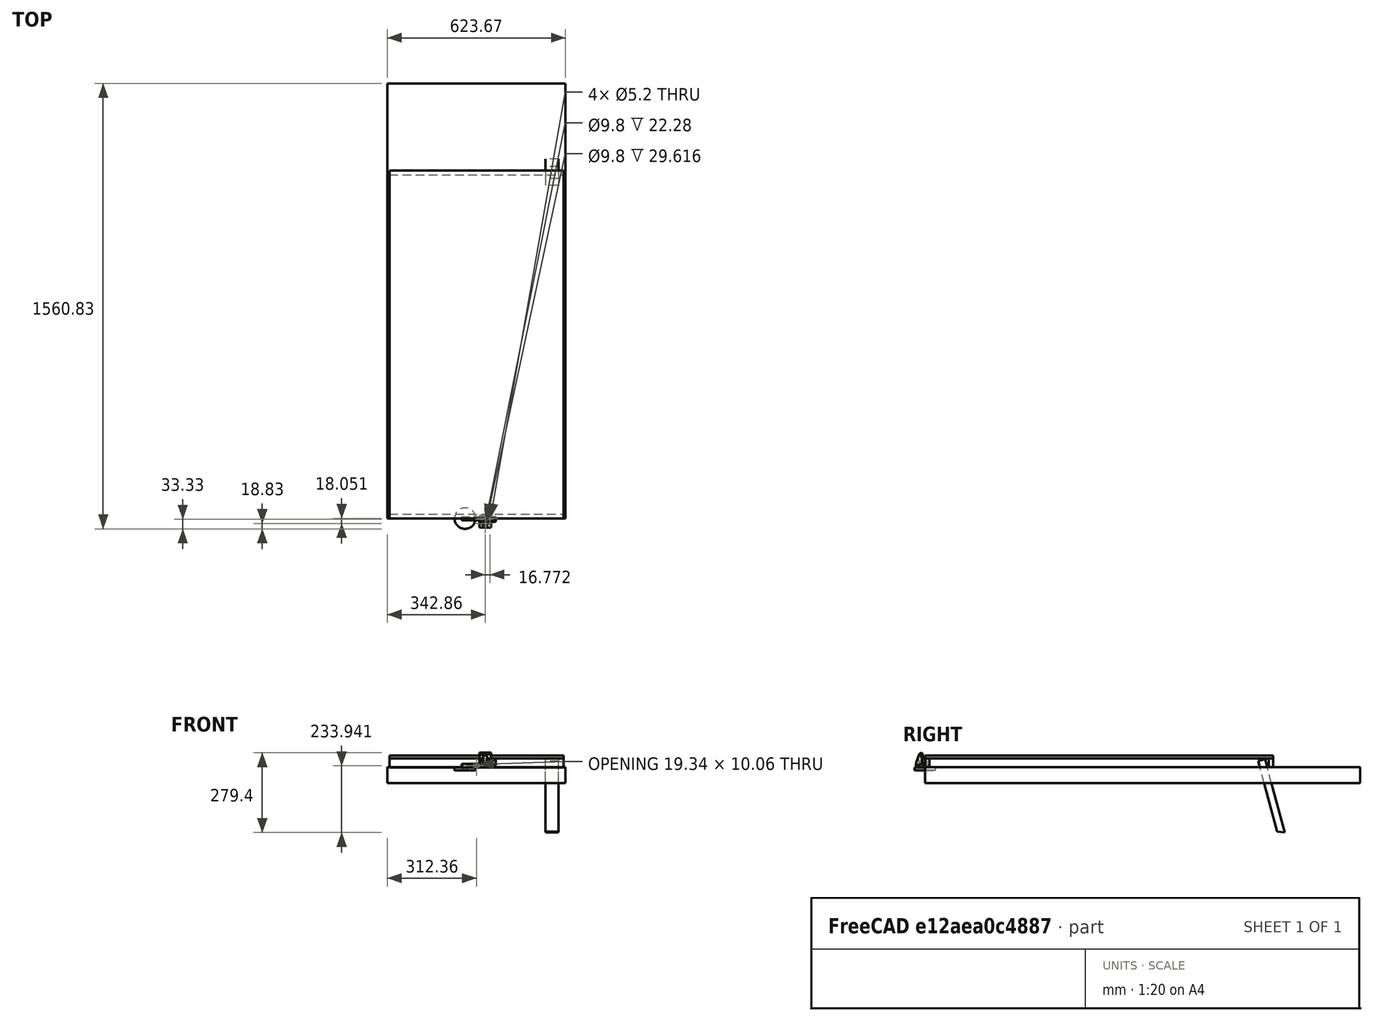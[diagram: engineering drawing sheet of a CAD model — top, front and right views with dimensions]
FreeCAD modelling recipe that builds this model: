
FCSTD DOCUMENT  (FreeCAD 0.21R)
Label: BoardModel
License: All rights reserved
LicenseURL: http://en.wikipedia.org/wiki/All_rights_reserved
objects: Sketcher::SketchObject×23, PartDesign::Pocket×12, PartDesign::Pad×11, PartDesign::Body×9, Part::FeaturePython×4, App::Part×4, App::Link×3, Mesh::Feature×2
note: 82 computed .brp shape members not serialized (recipe doc carries the construction recipe); baked Part::Feature solids carry a one-line shape summary decoded from their .brp

FEATURE [Sketcher::SketchObject] Sketch
  FullyConstrained = true
  MapMode = 5
  Support = -> [XY_Plane]
  sketch-geometry (10):
    g0: LineSegment StartX=-52.3875 StartY=6.35 StartZ=0 EndX=52.3875 EndY=6.35 EndZ=0
    g1: LineSegment StartX=52.3875 StartY=6.35 StartZ=0 EndX=52.3875 EndY=-6.35 EndZ=0
    g2: LineSegment StartX=52.3875 StartY=-6.35 StartZ=0 EndX=-52.3875 EndY=-6.35 EndZ=0
    g3: LineSegment StartX=-52.3875 StartY=-6.35 StartZ=0 EndX=-52.3875 EndY=6.35 EndZ=0
    g4: Circle CenterX=-47.3875 CenterY=0 CenterZ=0 NormalX=0 NormalY=0 NormalZ=1 AngleXU=0 Radius=2.5
    g5: Circle CenterX=-32.8875 CenterY=0 CenterZ=0 NormalX=0 NormalY=0 NormalZ=1 AngleXU=0 Radius=2.5
    g6: Circle CenterX=32.8875 CenterY=0 CenterZ=0 NormalX=0 NormalY=0 NormalZ=1 AngleXU=0 Radius=2
    g7: Circle CenterX=47.3875 CenterY=0 CenterZ=0 NormalX=0 NormalY=0 NormalZ=1 AngleXU=0 Radius=2
    g8: LineSegment StartX=-47.3875 StartY=0 StartZ=0 EndX=-32.8875 EndY=0 EndZ=0
    g9: LineSegment StartX=32.8875 StartY=0 StartZ=0 EndX=47.3875 EndY=0 EndZ=0
  constraints (26):
    c: Coincident(g0,g1)
    c: Coincident(g1,g2)
    c: Coincident(g2,g3)
    c: Coincident(g3,g0)
    c: Horizontal(g2)
    c: Vertical(g1)
    c: Symmetric(g0,g0,g-2)
    c: DistanceY(g3,g3) = 12.7
    c: Symmetric(g0,g2,g-1)
    c: DistanceX(g0,g0) = 104.775
    c: PointOnObject(g4,g-1)
    c: PointOnObject(g5,g-1)
    c: PointOnObject(g6,g-1)
    c: PointOnObject(g7,g-1)
    c: Diameter(g6) = 4
    c: Equal(g7,g6)
    c: Equal(g5,g4)
    c: Coincident(g8,g4)
    c: Coincident(g8,g5)
    c: Coincident(g9,g6)
    c: Coincident(g9,g7)
    c: Equal(g9,g8)
    c: Diameter(g5) = 5
    c: DistanceX(g8,g8) = 14.5
    c: DistanceX(g0,g4) = 5
    c: DistanceX(g7,g0) = 5
FEATURE [PartDesign::Pad] Pad
  Direction = (0,0,1)
  Length = 12.7
  Length2 = 10
  Profile = -> Sketch
  ReferenceAxis = -> Sketch [N_Axis]
  Type = 0
FEATURE [Sketcher::SketchObject] Sketch001
  FullyConstrained = false
  MapMode = 5
  Support = -> [XY_Plane001]
  sketch-geometry (3):
    g0: Circle CenterX=0 CenterY=0 CenterZ=0 NormalX=0 NormalY=0 NormalZ=1 AngleXU=0 Radius=36.8321
    g1: Circle CenterX=-7.25 CenterY=0 CenterZ=0 NormalX=0 NormalY=0 NormalZ=1 AngleXU=0 Radius=2.1
    g2: Circle CenterX=7.25 CenterY=0 CenterZ=0 NormalX=0 NormalY=0 NormalZ=1 AngleXU=0 Radius=2.1
  constraints (6):
    c: Coincident(g0,g-1)
    c: PointOnObject(g1,g-1)
    c: Equal(g1,g2)
    c: Symmetric(g1,g2,g0)
    c: DistanceX(g1,g2) = 14.5
    c: Diameter(g2) = 4.2
FEATURE [Sketcher::SketchObject] Sketch002
  FullyConstrained = true
  MapMode = 5
  Placement = pos=(0,0,0) rot=(0.57735,0.57735,0.57735;2.0944rad)
  Support = -> [YZ_Plane003]
  sketch-geometry (4):
    g0: LineSegment StartX=0 StartY=0 StartZ=0 EndX=15.24 EndY=0 EndZ=0
    g1: LineSegment StartX=15.24 StartY=0 StartZ=0 EndX=15.24 EndY=31.75 EndZ=0
    g2: LineSegment StartX=15.24 StartY=31.75 StartZ=0 EndX=0 EndY=31.75 EndZ=0
    g3: LineSegment StartX=0 StartY=31.75 StartZ=0 EndX=0 EndY=0 EndZ=0
  constraints (11):
    c: Coincident(g0,g1)
    c: Coincident(g1,g2)
    c: Coincident(g2,g3)
    c: Coincident(g3,g0)
    c: Horizontal(g0)
    c: Horizontal(g2)
    c: Vertical(g1)
    c: Vertical(g3)
    c: Coincident(g0,g-1)
    c: DistanceY(g3,g3) = 31.75
    c: DistanceX(g0,g0) = 15.24
FEATURE [PartDesign::Pad] Pad001
  Direction = (1,-2e-16,3e-16)
  Length = 609.6
  Length2 = 10
  Midplane = true
  Placement = pos=(0,0,0) rot=(0.57735,0.57735,0.57735;2.0944rad)
  Profile = -> Sketch002
  ReferenceAxis = -> Sketch002 [N_Axis]
  Type = 0
FEATURE [PartDesign::Body] Body002  label="Front"
  Group = -> [Sketch002,Pad001]
  Origin = -> Origin003
  Tip = -> Pad001
FEATURE [PartDesign::Pad] Pad002
  Direction = (0,0,1)
  Length = 10
  Length2 = 10
  Profile = -> Sketch001
  ReferenceAxis = -> Sketch001 [N_Axis]
  Reversed = true
  Type = 0
FEATURE [Sketcher::SketchObject] Sketch003
  AttachmentOffset = pos=(0,0,31.75) rot=(0,0,1;0rad)
  FullyConstrained = true
  MapMode = 5
  Placement = pos=(0,0,31.75) rot=(0,0,1;0rad)
  Support = -> [XY_Plane005]
  sketch-geometry (4):
    g0: LineSegment StartX=-304.8 StartY=0 StartZ=0 EndX=304.8 EndY=0 EndZ=0
    g1: LineSegment StartX=304.8 StartY=0 StartZ=0 EndX=304.8 EndY=1219.2 EndZ=0
    g2: LineSegment StartX=304.8 StartY=1219.2 StartZ=0 EndX=-304.8 EndY=1219.2 EndZ=0
    g3: LineSegment StartX=-304.8 StartY=1219.2 StartZ=0 EndX=-304.8 EndY=0 EndZ=0
  constraints (11):
    c: Coincident(g0,g1)
    c: Coincident(g1,g2)
    c: Coincident(g2,g3)
    c: Coincident(g3,g0)
    c: Horizontal(g2)
    c: Vertical(g1)
    c: Vertical(g3)
    c: Symmetric(g0,g0,g-2)
    c: DistanceX(g0,g0) = 609.6
    c: DistanceY(g3,g3) = 1219.2
    c: PointOnObject(g0,g-1)
FEATURE [PartDesign::Pad] Pad003
  Direction = (0,0,1)
  Length = 10
  Length2 = 10
  Profile = -> Sketch003
  ReferenceAxis = -> Sketch003 [N_Axis]
  Type = 0
FEATURE [PartDesign::Body] Body003  label="Top"
  Group = -> [Sketch003,Pad003]
  Origin = -> Origin005
  Tip = -> Pad003
FEATURE [Sketcher::SketchObject] Sketch004
  FullyConstrained = false
  MapMode = 5
  Placement = pos=(0,0,0) rot=(0.57735,0.57735,0.57735;2.0944rad)
  Support = -> [YZ_Plane006]
  sketch-geometry (8):
    g0: LineSegment StartX=-1.51635 StartY=-5.19268 StartZ=0 EndX=-5.92453 EndY=19.8073 EndZ=0
    g1: LineSegment StartX=12.7 StartY=8 StartZ=0 EndX=12.7 EndY=0 EndZ=0
    g2: LineSegment StartX=0 StartY=0 StartZ=0 EndX=12.7 EndY=0 EndZ=0
    g3: LineSegment StartX=12.7 StartY=8 StartZ=0 EndX=0.357421 EndY=8 EndZ=0
    g4: LineSegment StartX=0.357421 StartY=8 StartZ=0 EndX=-1.72453 EndY=19.8073 EndZ=0
    g5: LineSegment StartX=-1.72453 StartY=19.8073 StartZ=0 EndX=-5.92453 EndY=19.8073 EndZ=0
    g6: LineSegment StartX=-1.51635 StartY=-5.19268 StartZ=0 EndX=0 EndY=-5.19268 EndZ=0
    g7: LineSegment StartX=0 StartY=-5.19268 StartZ=0 EndX=0 EndY=0 EndZ=0
  constraints (21):
    c: PointOnObject(g1,g-1)
    c: Vertical(g1)
    c: Coincident(g1,g2)
    c: Angle(g-1,g0) = 1.74533
    c: DistanceY(g0,g0) = 25
    c: Coincident(g3,g1)
    c: Horizontal(g3)
    c: Coincident(g4,g3)
    c: Coincident(g5,g0)
    c: Horizontal(g5)
    c: Coincident(g6,g0)
    c: PointOnObject(g6,g-2)
    c: Horizontal(g6)
    c: Coincident(g7,g6)
    c: Coincident(g7,g2)
    c: Vertical(g7)
    c: Parallel(g4,g0)
    c: Coincident(g4,g5)
    c: DistanceY(g1,g1) = 8
    c: DistanceX(g5,g5) = 4.2
    c: DistanceX(g2,g2) = 12.7
FEATURE [PartDesign::Pad] Pad004
  Direction = (1,-2e-16,3e-16)
  Length = 55
  Length2 = 10
  Placement = pos=(0,0,0) rot=(0.57735,0.57735,0.57735;2.0944rad)
  Profile = -> Sketch004
  ReferenceAxis = -> Sketch004 [N_Axis]
  Type = 0
FEATURE [Sketcher::SketchObject] Sketch005
  AttachmentOffset = pos=(0,0,2) rot=(1,0,0;-0.174533rad)
  FullyConstrained = false
  MapMode = 5
  Placement = pos=(0,2,4e-16) rot=(0,-0.642788,-0.766044;3.14159rad)
  Support = -> [XZ_Plane006]
  sketch-geometry (5):
    g0: Circle CenterX=-44.4755 CenterY=12.9253 CenterZ=0 NormalX=0 NormalY=0 NormalZ=1 AngleXU=0 Radius=2.5
    g1: Circle CenterX=-10.5245 CenterY=12.9253 CenterZ=0 NormalX=0 NormalY=0 NormalZ=1 AngleXU=0 Radius=2.5
    g2: LineSegment StartX=-55 StartY=24.7239 StartZ=0 EndX=-55 EndY=-16.9766 EndZ=0
    g3: LineSegment StartX=-44.4755 StartY=12.9253 StartZ=0 EndX=-55 EndY=12.9253 EndZ=0
    g4: LineSegment StartX=-10.5245 StartY=12.9253 StartZ=0 EndX=0 EndY=12.9253 EndZ=0
  constraints (12):
    c: Equal(g1,g0)
    c: Horizontal(g0,g1)
    c: Vertical(g2)
    c: DistanceX(g2,g-1) = 55
    c: Coincident(g3,g0)
    c: PointOnObject(g3,g2)
    c: Horizontal(g3)
    c: Coincident(g4,g1)
    c: Horizontal(g4)
    c: PointOnObject(g4,g-2)
    c: Equal(g4,g3)
    c: Diameter(g0) = 5
FEATURE [Sketcher::SketchObject] Sketch006
  AttachmentOffset = pos=(0,0,-10) rot=(0,0,1;0rad)
  FullyConstrained = false
  MapMode = 5
  Placement = pos=(0,0,-10) rot=(0,0,1;0rad)
  Support = -> [XY_Plane001]
  sketch-geometry (3):
    g0: Circle CenterX=0 CenterY=0 CenterZ=0 NormalX=0 NormalY=0 NormalZ=1 AngleXU=0 Radius=36.8321
    g1: Circle CenterX=-7.25 CenterY=0 CenterZ=0 NormalX=0 NormalY=0 NormalZ=1 AngleXU=0 Radius=3.75
    g2: Circle CenterX=7.25 CenterY=0 CenterZ=0 NormalX=0 NormalY=0 NormalZ=1 AngleXU=0 Radius=3.75
  constraints (6):
    c: Coincident(g0,g-1)
    c: PointOnObject(g1,g-1)
    c: Equal(g1,g2)
    c: Symmetric(g1,g2,g0)
    c: DistanceX(g1,g2) = 14.5
    c: Diameter(g2) = 7.5
FEATURE [PartDesign::Pocket] Pocket001
  BaseFeature = -> Pad002
  Direction = (0,0,-1)
  Length = 5
  Length2 = 5
  Profile = -> Sketch006
  ReferenceAxis = -> Sketch006 [N_Axis]
  Reversed = true
  Type = 0
FEATURE [PartDesign::Body] Body001  label="Foot"
  Group = -> [Sketch001,Pad002,Sketch006,Pocket001]
  Origin = -> Origin001
  Placement = pos=(-40.005,0,0) rot=(0,0,1;0rad)
  Tip = -> Pocket001
FEATURE [Sketcher::SketchObject] Sketch007
  FullyConstrained = false
  MapMode = 5
  Support = -> [XY_Plane006]
  sketch-geometry (6):
    g0: Circle CenterX=20.25 CenterY=6.35 CenterZ=0 NormalX=0 NormalY=0 NormalZ=1 AngleXU=0 Radius=2.6
    g1: Circle CenterX=34.75 CenterY=6.35 CenterZ=0 NormalX=0 NormalY=0 NormalZ=1 AngleXU=0 Radius=2.6
    g2: LineSegment StartX=40.5 StartY=12.7 StartZ=0 EndX=35.9057 EndY=12.7 EndZ=0
    g3: LineSegment StartX=20.25 StartY=6.35 StartZ=0 EndX=34.75 EndY=6.35 EndZ=0
    g4: LineSegment StartX=55 StartY=10.9102 StartZ=0 EndX=55 EndY=0 EndZ=0
    g5: LineSegment StartX=27.5 StartY=6.35 StartZ=0 EndX=27.5 EndY=0 EndZ=0
  constraints (15):
    c: Horizontal(g1,g0)
    c: Equal(g1,g0)
    c: DistanceX(g0,g1) = 14.5
    c: Diameter(g1) = 5.2
    c: Horizontal(g2)
    c: DistanceY(g-1,g2) = 12.7
    c: Coincident(g3,g0)
    c: Coincident(g3,g1)
    c: Symmetric(g2,g-1,g0)
    c: PointOnObject(g4,g-1)
    c: Vertical(g4)
    c: DistanceX(g-1,g4) = 55
    c: Vertical(g5)
    c: Symmetric(g-1,g4,g5)
    c: Symmetric(g0,g1,g5)
FEATURE [PartDesign::Pocket] Pocket
  BaseFeature = -> Pad004
  Direction = (0,0,-1)
  Length = 10
  Length2 = 5
  Placement = pos=(0,0,0) rot=(0.57735,0.57735,0.57735;2.0944rad)
  Profile = -> Sketch007
  ReferenceAxis = -> Sketch007 [N_Axis]
  Reversed = true
  Type = 0
FEATURE [PartDesign::Pocket] Pocket002
  BaseFeature = -> Pocket
  Direction = (0,-0.984808,-0.173648)
  Length = 5
  Length2 = 5
  Placement = pos=(0,0,0) rot=(0.57735,0.57735,0.57735;2.0944rad)
  Profile = -> Sketch005
  ReferenceAxis = -> Sketch005 [N_Axis]
  Type = 0
FEATURE [Sketcher::SketchObject] Sketch008
  AttachmentOffset = pos=(0,0,4) rot=(0,0,1;0rad)
  FullyConstrained = false
  MapMode = 5
  Placement = pos=(0,0,4) rot=(0,0,1;0rad)
  Support = -> [XY_Plane006]
  sketch-geometry (6):
    g0: Circle CenterX=20.25 CenterY=6.35 CenterZ=0 NormalX=0 NormalY=0 NormalZ=1 AngleXU=0 Radius=4.4
    g1: Circle CenterX=34.75 CenterY=6.35 CenterZ=0 NormalX=0 NormalY=0 NormalZ=1 AngleXU=0 Radius=4.4
    g2: LineSegment StartX=40.5 StartY=12.7 StartZ=0 EndX=35.9057 EndY=12.7 EndZ=0
    g3: LineSegment StartX=20.25 StartY=6.35 StartZ=0 EndX=34.75 EndY=6.35 EndZ=0
    g4: LineSegment StartX=55 StartY=10.9102 StartZ=0 EndX=55 EndY=0 EndZ=0
    g5: LineSegment StartX=27.5 StartY=6.35 StartZ=0 EndX=27.5 EndY=0 EndZ=0
  constraints (15):
    c: Horizontal(g1,g0)
    c: Equal(g1,g0)
    c: DistanceX(g0,g1) = 14.5
    c: Diameter(g1) = 8.8
    c: Horizontal(g2)
    c: DistanceY(g-1,g2) = 12.7
    c: Coincident(g3,g0)
    c: Coincident(g3,g1)
    c: Symmetric(g2,g-1,g0)
    c: PointOnObject(g4,g-1)
    c: Vertical(g4)
    c: DistanceX(g-1,g4) = 55
    c: Vertical(g5)
    c: Symmetric(g-1,g4,g5)
    c: Symmetric(g0,g1,g5)
FEATURE [PartDesign::Pocket] Pocket003
  BaseFeature = -> Pocket002
  Direction = (0,0,-1)
  Length = 5
  Length2 = 5
  Placement = pos=(0,0,0) rot=(0.57735,0.57735,0.57735;2.0944rad)
  Profile = -> Sketch008
  ReferenceAxis = -> Sketch008 [N_Axis]
  Reversed = true
  Type = 0
FEATURE [Sketcher::SketchObject] Sketch009
  FullyConstrained = false
  MapMode = 5
  Placement = pos=(0,0,0) rot=(0.57735,0.57735,0.57735;2.0944rad)
  Support = -> [YZ_Plane006]
  sketch-geometry (11):
    g0: LineSegment StartX=-1.51635 StartY=-5.19267 StartZ=0 EndX=-5.92453 EndY=19.8073 EndZ=0
    g1: LineSegment StartX=12.7 StartY=8 StartZ=0 EndX=12.7 EndY=0 EndZ=0
    g2: LineSegment StartX=0 StartY=0 StartZ=0 EndX=12.7 EndY=0 EndZ=0
    g3: LineSegment StartX=12.7 StartY=8 StartZ=0 EndX=0.357421 EndY=8 EndZ=0
    g4: LineSegment StartX=0.357421 StartY=8 StartZ=0 EndX=-1.72453 EndY=19.8073 EndZ=0
    g5: LineSegment StartX=-1.72453 StartY=19.8073 StartZ=0 EndX=-5.92453 EndY=19.8073 EndZ=0
    g6: LineSegment StartX=-1.51635 StartY=-5.19267 StartZ=0 EndX=0 EndY=-5.19267 EndZ=0
    g7: LineSegment StartX=0 StartY=-5.19267 StartZ=0 EndX=0 EndY=0 EndZ=0
    g8: LineSegment StartX=-1.72453 StartY=19.8073 StartZ=0 EndX=2.33774 EndY=19.8073 EndZ=0
    g9: LineSegment StartX=12.7 StartY=9.44507 StartZ=0 EndX=12.7 EndY=8 EndZ=0
    g10: ArcOfCircle CenterX=2.33774 CenterY=9.44507 CenterZ=0 NormalX=0 NormalY=0 NormalZ=1 AngleXU=0 Radius=10.3623 StartAngle=0 EndAngle=1.5708
  constraints (29):
    c: PointOnObject(g1,g-1)
    c: Vertical(g1)
    c: Coincident(g1,g2)
    c: Angle(g-1,g0) = 1.74533
    c: DistanceY(g0,g0) = 25
    c: Coincident(g3,g1)
    c: Horizontal(g3)
    c: Coincident(g4,g3)
    c: Coincident(g5,g0)
    c: Horizontal(g5)
    c: Coincident(g6,g0)
    c: PointOnObject(g6,g-2)
    c: Horizontal(g6)
    c: Coincident(g7,g6)
    c: Coincident(g7,g2)
    c: Vertical(g7)
    c: Parallel(g4,g0)
    c: Coincident(g4,g5)
    c: DistanceY(g1,g1) = 8
    c: DistanceX(g5,g5) = 4.2
    c: DistanceX(g2,g2) = 12.7
    c: DistanceX(g3) = 0.357421
    c: DistanceX(g4) = -1.72453
    c: Coincident(g8,g4)
    c: Horizontal(g8)
    c: Coincident(g9,g1)
    c: Vertical(g9)
    c: Tangent(g8,g10) = 1.5708
    c: Tangent(g9,g10) = 1.5708
FEATURE [PartDesign::Pad] Pad005
  BaseFeature = -> Pocket003
  Direction = (1,-2e-16,3e-16)
  Length = 4
  Length2 = 10
  Placement = pos=(0,0,0) rot=(0.57735,0.57735,0.57735;2.0944rad)
  Profile = -> Sketch009
  ReferenceAxis = -> Sketch009 [N_Axis]
  Type = 0
FEATURE [Sketcher::SketchObject] Sketch010
  AttachmentOffset = pos=(0,0,55) rot=(0,0,1;0rad)
  FullyConstrained = false
  MapMode = 5
  Placement = pos=(55,-1.22e-14,1.22e-14) rot=(0.57735,0.57735,0.57735;2.0944rad)
  Support = -> [YZ_Plane006]
  sketch-geometry (11):
    g0: LineSegment StartX=-1.51635 StartY=-5.19267 StartZ=0 EndX=-5.92453 EndY=19.8073 EndZ=0
    g1: LineSegment StartX=12.7 StartY=8 StartZ=0 EndX=12.7 EndY=0 EndZ=0
    g2: LineSegment StartX=0 StartY=0 StartZ=0 EndX=12.7 EndY=0 EndZ=0
    g3: LineSegment StartX=12.7 StartY=8 StartZ=0 EndX=0.357421 EndY=8 EndZ=0
    g4: LineSegment StartX=0.357421 StartY=8 StartZ=0 EndX=-1.72453 EndY=19.8073 EndZ=0
    g5: LineSegment StartX=-1.72453 StartY=19.8073 StartZ=0 EndX=-5.92453 EndY=19.8073 EndZ=0
    g6: LineSegment StartX=-1.51635 StartY=-5.19267 StartZ=0 EndX=0 EndY=-5.19267 EndZ=0
    g7: LineSegment StartX=0 StartY=-5.19267 StartZ=0 EndX=0 EndY=0 EndZ=0
    g8: LineSegment StartX=-1.72453 StartY=19.8073 StartZ=0 EndX=2.33774 EndY=19.8073 EndZ=0
    g9: LineSegment StartX=12.7 StartY=9.44507 StartZ=0 EndX=12.7 EndY=8 EndZ=0
    g10: ArcOfCircle CenterX=2.33774 CenterY=9.44507 CenterZ=0 NormalX=0 NormalY=0 NormalZ=1 AngleXU=0 Radius=10.3623 StartAngle=0 EndAngle=1.5708
  constraints (29):
    c: PointOnObject(g1,g-1)
    c: Vertical(g1)
    c: Coincident(g1,g2)
    c: Angle(g-1,g0) = 1.74533
    c: DistanceY(g0,g0) = 25
    c: Coincident(g3,g1)
    c: Horizontal(g3)
    c: Coincident(g4,g3)
    c: Coincident(g5,g0)
    c: Horizontal(g5)
    c: Coincident(g6,g0)
    c: PointOnObject(g6,g-2)
    c: Horizontal(g6)
    c: Coincident(g7,g6)
    c: Coincident(g7,g2)
    c: Vertical(g7)
    c: Parallel(g4,g0)
    c: Coincident(g4,g5)
    c: DistanceY(g1,g1) = 8
    c: DistanceX(g5,g5) = 4.2
    c: DistanceX(g2,g2) = 12.7
    c: DistanceX(g3) = 0.357421
    c: DistanceX(g4) = -1.72453
    c: Coincident(g8,g4)
    c: Horizontal(g8)
    c: Coincident(g9,g1)
    c: Vertical(g9)
    c: Tangent(g8,g10) = 1.5708
    c: Tangent(g9,g10) = 1.5708
FEATURE [PartDesign::Pad] Pad006
  BaseFeature = -> Pad005
  Direction = (1,-2e-16,3e-16)
  Length = 4
  Length2 = 10
  Placement = pos=(0,0,0) rot=(0.57735,0.57735,0.57735;2.0944rad)
  Profile = -> Sketch010
  ReferenceAxis = -> Sketch010 [N_Axis]
  Reversed = true
  Type = 0
FEATURE [Part::FeaturePython] Screw  label="M5x8-Screw"  # Fasteners workbench fastener (typed FeaturePython)
  Placement = pos=(47.2694,0,16.891) rot=(0,0,1;0rad)
  diameter = 6
  invert = false
  leftHanded = false
  length = 0
  lengthCustom = 8
  matchOuter = false
  offset = 0
  thread = false
  type = 36
FEATURE [Part::FeaturePython] Screw001  label="M5x8-Screw001"  # Fasteners workbench fastener (typed FeaturePython)
  Placement = pos=(32.7406,0,16.891) rot=(0,0,1;0rad)
  diameter = 6
  invert = false
  leftHanded = false
  length = 0
  lengthCustom = 8
  matchOuter = false
  offset = 0
  thread = false
  type = 36
FEATURE [Sketcher::SketchObject] Sketch011
  FullyConstrained = false
  MapMode = 5
  Placement = pos=(0,0,0) rot=(1,0,0;1.5708rad)
  Support = -> [XZ_Plane]
  sketch-geometry (2):
    g0: ArcOfCircle CenterX=-4.4394 CenterY=6.54104 CenterZ=0 NormalX=0 NormalY=0 NormalZ=1 AngleXU=0 Radius=5.22923 StartAngle=0.556784 EndAngle=5.7264
    g1: ArcOfCircle CenterX=4.4394 CenterY=6.54104 CenterZ=0 NormalX=0 NormalY=0 NormalZ=1 AngleXU=0 Radius=5.22923 StartAngle=3.69838 EndAngle=8.86799
  constraints (5):
    c: Equal(g1,g0)
    c: Vertical(g0,g0)
    c: Vertical(g1,g1)
    c: Symmetric(g1,g0,g-2)
    c: Coincident(g0,g1)
FEATURE [PartDesign::Pocket] Pocket004
  BaseFeature = -> Pad
  Direction = (0,1,2e-16)
  Length = 5
  Length2 = 5
  Midplane = true
  Profile = -> Sketch011
  ReferenceAxis = -> Sketch011 [N_Axis]
  Type = 1
FEATURE [PartDesign::Body] Body  label="Loadcell"
  Group = -> [Sketch,Pad,Sketch011,Pocket004]
  Origin = -> Origin
  Tip = -> Pocket004
FEATURE [Sketcher::SketchObject] Sketch012
  ExternalGeometry = -> [Pad006]
  FullyConstrained = false
  MapMode = 5
  Placement = pos=(5.6e-15,12.7,-2.8e-15) rot=(0.57735,0.57735,0.57735;4.18879rad)
  Support = -> [Pad006]
  sketch-geometry (10):
    g0: LineSegment StartX=0 StartY=43.1845 StartZ=0 EndX=3.04874 EndY=43.1845 EndZ=0
    g1: LineSegment StartX=3.04874 StartY=55 StartZ=0 EndX=-3.04704 EndY=55 EndZ=0
    g2: LineSegment StartX=-3.04704 StartY=55 StartZ=0 EndX=-3.04704 EndY=0 EndZ=0
    g3: LineSegment StartX=-3.04704 StartY=0 StartZ=0 EndX=0 EndY=0 EndZ=0
    g4: LineSegment StartX=0 StartY=0 StartZ=0 EndX=3.04874 EndY=0 EndZ=0
    g5: LineSegment StartX=3.04874 StartY=0 StartZ=0 EndX=3.04874 EndY=11.8155 EndZ=0
    g6: LineSegment StartX=3.04874 StartY=11.8155 StartZ=0 EndX=0 EndY=11.8155 EndZ=0
    g7: LineSegment StartX=0 StartY=11.8155 StartZ=0 EndX=0 EndY=43.1845 EndZ=0
    g8: LineSegment StartX=-3.04704 StartY=27.5 StartZ=0 EndX=7.44408 EndY=27.5 EndZ=0
    g9: LineSegment StartX=3.04874 StartY=55 StartZ=0 EndX=3.04874 EndY=43.1845 EndZ=0
  constraints (24):
    c: PointOnObject(g0,g-2)
    c: Horizontal(g0)
    c: Horizontal(g1)
    c: Coincident(g2,g1)
    c: PointOnObject(g2,g-1)
    c: Vertical(g2)
    c: Coincident(g3,g2)
    c: Coincident(g3,g-1)
    c: Coincident(g4,g3)
    c: PointOnObject(g4,g-1)
    c: Coincident(g5,g4)
    c: Vertical(g5)
    c: Coincident(g6,g5)
    c: Horizontal(g6)
    c: PointOnObject(g6,g-2)
    c: Coincident(g7,g6)
    c: Coincident(g7,g0)
    c: Equal(g0,g6)
    c: Symmetric(g1,g2,g8)
    c: Symmetric(g0,g5,g8)
    c: Coincident(g9,g1)
    c: Coincident(g9,g0)
    c: Vertical(g9)
    c: PointOnObject(g1,g-3)
FEATURE [PartDesign::Pocket] Pocket005
  BaseFeature = -> Pad006
  Direction = (-8e-16,-1,1e-16)
  Length = 0
  Length2 = 5
  Placement = pos=(0,0,0) rot=(0.57735,0.57735,0.57735;2.0944rad)
  Profile = -> Sketch012
  ReferenceAxis = -> Sketch012 [N_Axis]
  Type = 3
  UpToFace = -> Pad006 [Face8]
FEATURE [PartDesign::Body] Body004  label="Mnt"
  Group = -> [Sketch004,Pad004,Sketch005,Sketch007,Pocket,Pocket002,Sketch008,Pocket003,Sketch009,Pad005,Sketch010,Pad006,Sketch012,Pocket005]
  Origin = -> Origin006
  Placement = pos=(12.5222,-6.2992,12.7254) rot=(0,0,1;0rad)
  Tip = -> Pocket005
FEATURE [App::Part] Part001  label="FootAssembly"
  Group = -> [Body001,Body,Body004,Screw,Screw001]
  Origin = -> Origin004
  Placement = pos=(-225.882,27.2796,14.5542) rot=(0,0,1;0rad)
FEATURE [Mesh::Feature] Mesh  label="Mnt (Meshed)"
FEATURE [Mesh::Feature] Mesh001  label="Foot (Meshed)"
FEATURE [Sketcher::SketchObject] Sketch013
  FullyConstrained = true
  MapMode = 5
  Placement = pos=(0,0,0) rot=(0.57735,0.57735,0.57735;2.0944rad)
  Support = -> [YZ_Plane007]
  sketch-geometry (4):
    g0: LineSegment StartX=0 StartY=0 StartZ=0 EndX=15.24 EndY=0 EndZ=0
    g1: LineSegment StartX=15.24 StartY=0 StartZ=0 EndX=15.24 EndY=31.75 EndZ=0
    g2: LineSegment StartX=15.24 StartY=31.75 StartZ=0 EndX=0 EndY=31.75 EndZ=0
    g3: LineSegment StartX=0 StartY=31.75 StartZ=0 EndX=0 EndY=0 EndZ=0
  constraints (11):
    c: Coincident(g0,g1)
    c: Coincident(g1,g2)
    c: Coincident(g2,g3)
    c: Coincident(g3,g0)
    c: Horizontal(g0)
    c: Horizontal(g2)
    c: Vertical(g1)
    c: Vertical(g3)
    c: Coincident(g0,g-1)
    c: DistanceY(g3,g3) = 31.75
    c: DistanceX(g0,g0) = 15.24
FEATURE [PartDesign::Pad] Pad007
  Direction = (1,-2e-16,3e-16)
  Length = 609.6
  Length2 = 10
  Midplane = true
  Placement = pos=(0,0,0) rot=(0.57735,0.57735,0.57735;2.0944rad)
  Profile = -> Sketch013
  ReferenceAxis = -> Sketch013 [N_Axis]
  Type = 0
FEATURE [PartDesign::Body] Body005  label="Back"
  Group = -> [Sketch013,Pad007]
  Origin = -> Origin007
  Placement = pos=(0,1204,0) rot=(0,0,1;0rad)
  Tip = -> Pad007
FEATURE [Sketcher::SketchObject] Sketch014
  FullyConstrained = true
  MapMode = 5
  Placement = pos=(0,0,0) rot=(-0.57735,0.57735,0.57735;4.18879rad)
  Support = -> [YZ_Plane008]
  sketch-geometry (4):
    g0: LineSegment StartX=-12.55 StartY=0 StartZ=0 EndX=-12.55 EndY=266.7 EndZ=0
    g1: LineSegment StartX=-12.55 StartY=0 StartZ=0 EndX=12.55 EndY=10.16 EndZ=0
    g2: LineSegment StartX=12.55 StartY=10.16 StartZ=0 EndX=12.55 EndY=266.7 EndZ=0
    g3: LineSegment StartX=-12.55 StartY=266.7 StartZ=0 EndX=12.55 EndY=266.7 EndZ=0
  constraints (11):
    c: PointOnObject(g0,g-1)
    c: Vertical(g0)
    c: Coincident(g1,g0)
    c: Coincident(g2,g1)
    c: Vertical(g2)
    c: Coincident(g3,g0)
    c: Coincident(g3,g2)
    c: Symmetric(g0,g2,g-2)
    c: DistanceY(g0,g0) = 266.7
    c: DistanceY(g2,g2) = 256.54
    c: DistanceX(g0,g1) = 25.1
FEATURE [PartDesign::Pad] Pad008
  Direction = (-1,2e-16,-3e-16)
  Length = 45
  Length2 = 10
  Placement = pos=(0,0,0) rot=(0.57735,0.57735,0.57735;2.0944rad)
  Profile = -> Sketch014
  ReferenceAxis = -> Sketch014 [N_Axis]
  Type = 0
FEATURE [PartDesign::Body] Body006  label="Leg"
  Group = -> [Sketch014,Pad008]
  Origin = -> Origin008
  Placement = pos=(287,1247.47,-230.644) rot=(1,0,0;0.261799rad)
  Tip = -> Pad008
FEATURE [App::Link] Link  label="Leg001"
  LinkPlacement = pos=(-535.5,-0.00017282,3.69421e-05) rot=(1,0,0;0rad)
  LinkTransform = true
  LinkedObject = -> Body006
  Placement = pos=(-535.5,-0.00017282,3.69421e-05) rot=(1,0,0;0rad)
FEATURE [App::Part] Part  label="Board"
  Group = -> [Body002,Body003,Body005,Body006,Link]
  Origin = -> Origin002
  Placement = pos=(0,-3.74471,20.7985) rot=(1,0,0;0.174533rad)
FEATURE [Sketcher::SketchObject] Sketch015
  FullyConstrained = false
  MapMode = 5
  Placement = pos=(0,0,0) rot=(1,0,0;1.5708rad)
  Support = -> [XZ_Plane010]
  sketch-geometry (4):
    g0: LineSegment StartX=-312.359 StartY=1.62053 StartZ=0 EndX=311.309 EndY=1.62053 EndZ=0
    g1: LineSegment StartX=311.309 StartY=1.62053 StartZ=0 EndX=311.309 EndY=-54.3871 EndZ=0
    g2: LineSegment StartX=311.309 StartY=-54.3871 StartZ=0 EndX=-312.359 EndY=-54.3871 EndZ=0
    g3: LineSegment StartX=-312.359 StartY=-54.3871 StartZ=0 EndX=-312.359 EndY=1.62053 EndZ=0
  constraints (8):
    c: Coincident(g0,g1)
    c: Coincident(g1,g2)
    c: Coincident(g2,g3)
    c: Coincident(g3,g0)
    c: Horizontal(g0)
    c: Horizontal(g2)
    c: Vertical(g1)
    c: Vertical(g3)
FEATURE [PartDesign::Pad] Pad009
  Direction = (0,-1,2e-16)
  Length = 1524
  Length2 = 10
  Placement = pos=(0,0,0) rot=(1,0,0;1.5708rad)
  Profile = -> Sketch015
  ReferenceAxis = -> Sketch015 [N_Axis]
  Reversed = true
  Type = 0
FEATURE [PartDesign::Body] Body007
  Group = -> [Sketch015,Pad009]
  Origin = -> Origin010
  Tip = -> Pad009
FEATURE [App::Part] Part002  label="Floor"
  Group = -> [Body007]
  Origin = -> Origin009
  Placement = pos=(0,-107.5,0) rot=(0,0,1;0rad)
FEATURE [App::Link] Link001  label="Loadcell001"
  LinkPlacement = pos=(30.5001,-50.9996,0) rot=(0,0,1;1.5708rad)
  LinkedObject = -> Body
  Placement = pos=(30.5001,-50.9996,0) rot=(0,0,1;1.5708rad)
FEATURE [Sketcher::SketchObject] Sketch016
  FullyConstrained = false
  MapMode = 5
  Placement = pos=(0,0,0) rot=(0.57735,0.57735,0.57735;2.0944rad)
  Support = -> [YZ_Plane013]
  sketch-geometry (11):
    g0: LineSegment StartX=23.3154 StartY=0 StartZ=0 EndX=0 EndY=50 EndZ=0
    g1: LineSegment StartX=0 StartY=50 StartZ=0 EndX=-9.06308 EndY=45.7738 EndZ=0
    g2: LineSegment StartX=-6 StartY=25.3407 StartZ=0 EndX=-6 EndY=0 EndZ=0
    g3: LineSegment StartX=8.5 StartY=25.3407 StartZ=0 EndX=8.5 EndY=0 EndZ=0
    g4: LineSegment StartX=-10.9 StartY=20 StartZ=0 EndX=-1.1 EndY=20 EndZ=0
    g5: LineSegment StartX=3.6 StartY=20 StartZ=0 EndX=13.4 EndY=20 EndZ=0
    g6: LineSegment StartX=23.3154 StartY=0 StartZ=0 EndX=-20 EndY=0 EndZ=0
    g7: LineSegment StartX=-20 StartY=0 StartZ=0 EndX=-20 EndY=12 EndZ=0
    g8: LineSegment StartX=-26.8019 StartY=10.8 StartZ=0 EndX=-14.4043 EndY=10.8 EndZ=0
    g9: LineSegment StartX=-20 StartY=12 StartZ=0 EndX=-9.06308 EndY=45.7738 EndZ=0
    g10: LineSegment StartX=13.75 StartY=0 StartZ=0 EndX=13.75 EndY=10.7671 EndZ=0
  constraints (33):
    c: PointOnObject(g0,g-1)
    c: Coincident(g1,g0)
    c: Vertical(g2)
    c: Vertical(g3)
    c: DistanceX(g2,g3) = 14.5
    c: Horizontal(g3,g2)
    c: Horizontal(g2,g3)
    c: DistanceY(g2,g4) = 20
    c: Symmetric(g4,g4,g2)
    c: Symmetric(g5,g5,g3)
    c: Horizontal(g4,g5)
    c: DistanceY(g-1,g0) = 50
    c: Distance(g1) = 10
    c: PointOnObject(g0,g-2)
    c: Coincident(g6,g0)
    c: PointOnObject(g6,g-1)
    c: Coincident(g7,g6)
    c: Vertical(g7)
    c: DistanceX(g6,g-1) = 20
    c: Equal(g5,g4)
    c: Horizontal(g8)
    c: Coincident(g9,g7)
    c: Coincident(g9,g1)
    c: Angle(g-2,g0) = 0.436332
    c: Perpendicular(g0,g1)
    c: DistanceY(g6,g7) = 12
    c: DistanceX(g5,g5) = 9.8
    c: DistanceY(g-1,g5) = 20
    c: DistanceX(g-1,g3) = 8.5
    c: PointOnObject(g10,g6)
    c: Vertical(g10)
    c: DistanceX(g6,g10) = 33.75
    c: DistanceY(g6,g8) = 10.8
FEATURE [Part::FeaturePython] Screw002  label="M5x20-Screw"  # Fasteners workbench fastener (typed FeaturePython)
  Placement = pos=(30.5,-3.5,22) rot=(0,0,1;0rad)
  diameter = 3
  invert = false
  leftHanded = false
  length = 5
  lengthCustom = 20
  matchOuter = false
  offset = 0
  thread = false
  type = 42
FEATURE [PartDesign::Pad] Pad010
  Direction = (1,-2e-16,3e-16)
  Length = 40
  Length2 = 10
  Midplane = true
  Placement = pos=(0,0,0) rot=(0.57735,0.57735,0.57735;2.0944rad)
  Profile = -> Sketch016
  ReferenceAxis = -> Sketch016 [N_Axis]
  Type = 0
FEATURE [Sketcher::SketchObject] Sketch017  label="CounterBore"
  AttachmentOffset = pos=(0,0,20) rot=(0,0,1;0rad)
  FullyConstrained = true
  MapMode = 5
  Placement = pos=(0,0,20) rot=(0,0,1;0rad)
  Support = -> [XY_Plane013]
  sketch-geometry (2):
    g0: Circle CenterX=0 CenterY=-6 CenterZ=0 NormalX=0 NormalY=0 NormalZ=1 AngleXU=0 Radius=4.9
    g1: Circle CenterX=0 CenterY=8.5 CenterZ=0 NormalX=0 NormalY=0 NormalZ=1 AngleXU=0 Radius=4.9
  constraints (6):
    c: PointOnObject(g0,g-2)
    c: PointOnObject(g1,g-2)
    c: Equal(g1,g0)
    c: Diameter(g1) = 9.8
    c: DistanceY(g0,g1) = 14.5
    c: DistanceY(g-1,g1) = 8.5
FEATURE [Sketcher::SketchObject] Sketch018
  AttachmentOffset = pos=(0,0,20) rot=(0,0,1;0rad)
  FullyConstrained = true
  MapMode = 5
  Placement = pos=(0,-20,-4.4e-15) rot=(1,0,0;1.5708rad)
  Support = -> [XZ_Plane013]
  sketch-geometry (4):
    g0: LineSegment StartX=-6.375 StartY=0 StartZ=0 EndX=6.375 EndY=0 EndZ=0
    g1: LineSegment StartX=6.375 StartY=0 StartZ=0 EndX=6.375 EndY=10.8 EndZ=0
    g2: LineSegment StartX=6.375 StartY=10.8 StartZ=0 EndX=-6.375 EndY=10.8 EndZ=0
    g3: LineSegment StartX=-6.375 StartY=10.8 StartZ=0 EndX=-6.375 EndY=0 EndZ=0
  constraints (11):
    c: Coincident(g0,g1)
    c: Coincident(g1,g2)
    c: Coincident(g2,g3)
    c: Coincident(g3,g0)
    c: Horizontal(g2)
    c: Vertical(g1)
    c: Vertical(g3)
    c: PointOnObject(g0,g-1)
    c: Symmetric(g0,g0,g-2)
    c: DistanceX(g0,g0) = 12.75
    c: DistanceY(g0,g1) = 10.8
FEATURE [PartDesign::Pocket] Pocket006
  BaseFeature = -> Pad010
  Direction = (0,1,-2e-16)
  Length = 33.75
  Length2 = 5
  Placement = pos=(0,0,0) rot=(0.57735,0.57735,0.57735;2.0944rad)
  Profile = -> Sketch018
  ReferenceAxis = -> Sketch018 [N_Axis]
  Type = 0
FEATURE [Sketcher::SketchObject] Sketch019
  AttachmentOffset = pos=(0,5,-13) rot=(1,0,0;0.436332rad)
  FullyConstrained = false
  MapMode = 5
  Placement = pos=(0,13,5) rot=(1,0,0;2.00713rad)
  Support = -> [XZ_Plane013]
  sketch-geometry (10):
    g0: LineSegment StartX=-29.4073 StartY=60.2052 StartZ=0 EndX=-7 EndY=60.2052 EndZ=0
    g1: LineSegment StartX=-7 StartY=60.2052 StartZ=0 EndX=-7 EndY=24.8017 EndZ=0
    g2: LineSegment StartX=-19.8017 StartY=12 StartZ=0 EndX=-29.4073 EndY=12 EndZ=0
    g3: LineSegment StartX=-29.4073 StartY=12 StartZ=0 EndX=-29.4073 EndY=60.2052 EndZ=0
    g4: LineSegment StartX=7 StartY=60.2052 StartZ=0 EndX=29.4073 EndY=60.2052 EndZ=0
    g5: LineSegment StartX=29.4073 StartY=60.2052 StartZ=0 EndX=29.4073 EndY=12 EndZ=0
    g6: LineSegment StartX=29.4073 StartY=12 StartZ=0 EndX=19.8017 EndY=12 EndZ=0
    g7: LineSegment StartX=7 StartY=24.8017 StartZ=0 EndX=7 EndY=60.2052 EndZ=0
    g8: ArcOfCircle CenterX=-19.8017 CenterY=24.8017 CenterZ=0 NormalX=0 NormalY=0 NormalZ=1 AngleXU=0 Radius=12.8017 StartAngle=4.71239 EndAngle=6.28319
    g9: ArcOfCircle CenterX=19.8017 CenterY=24.8017 CenterZ=0 NormalX=0 NormalY=0 NormalZ=1 AngleXU=0 Radius=12.8017 StartAngle=3.14159 EndAngle=4.71239
  constraints (23):
    c: Coincident(g0,g1)
    c: Coincident(g2,g3)
    c: Coincident(g3,g0)
    c: Horizontal(g0)
    c: Horizontal(g2)
    c: Vertical(g1)
    c: Vertical(g3)
    c: Coincident(g4,g5)
    c: Coincident(g5,g6)
    c: Coincident(g7,g4)
    c: Horizontal(g4)
    c: Horizontal(g6)
    c: Vertical(g5)
    c: Vertical(g7)
    c: Tangent(g2,g8) = 1.5708
    c: Tangent(g1,g8) = 1.5708
    c: Tangent(g7,g9) = 1.5708
    c: Tangent(g6,g9) = 1.5708
    c: Horizontal(g6,g2)
    c: Symmetric(g7,g1,g-2)
    c: Symmetric(g0,g4,g-2)
    c: DistanceY(g-1,g2) = 12
    c: DistanceX(g1,g7) = 14
FEATURE [PartDesign::Pocket] Pocket007
  BaseFeature = -> Pocket006
  Direction = (0,0.906308,0.422618)
  Length = 50
  Length2 = 5
  Placement = pos=(0,0,0) rot=(0.57735,0.57735,0.57735;2.0944rad)
  Profile = -> Sketch019
  ReferenceAxis = -> Sketch019 [N_Axis]
  Reversed = true
  Type = 0
FEATURE [PartDesign::Pocket] Pocket008
  BaseFeature = -> Pocket007
  Direction = (0,0,-1)
  Length = 30
  Length2 = 5
  Placement = pos=(0,0,0) rot=(0.57735,0.57735,0.57735;2.0944rad)
  Profile = -> Sketch017
  ReferenceAxis = -> Sketch017 [N_Axis]
  Reversed = true
  Type = 1
FEATURE [Sketcher::SketchObject] Sketch020  label="BoltHoles"
  AttachmentOffset = pos=(0,0,20) rot=(0,0,1;0rad)
  FullyConstrained = true
  MapMode = 5
  Placement = pos=(0,0,20) rot=(0,0,1;0rad)
  Support = -> [XY_Plane013]
  sketch-geometry (2):
    g0: Circle CenterX=0 CenterY=-6 CenterZ=0 NormalX=0 NormalY=0 NormalZ=1 AngleXU=0 Radius=2.6
    g1: Circle CenterX=0 CenterY=8.5 CenterZ=0 NormalX=0 NormalY=0 NormalZ=1 AngleXU=0 Radius=2.6
  constraints (6):
    c: PointOnObject(g0,g-2)
    c: PointOnObject(g1,g-2)
    c: Equal(g1,g0)
    c: Diameter(g1) = 5.2
    c: DistanceY(g0,g1) = 14.5
    c: DistanceY(g-1,g1) = 8.5
FEATURE [PartDesign::Pocket] Pocket009
  BaseFeature = -> Pocket008
  Direction = (0,0,-1)
  Length = 5
  Length2 = 5
  Placement = pos=(0,0,0) rot=(0.57735,0.57735,0.57735;2.0944rad)
  Profile = -> Sketch020
  ReferenceAxis = -> Sketch020 [N_Axis]
  Type = 1
FEATURE [App::Link] Link002  label="Foot001"
  LinkPlacement = pos=(29.5,-89.5001,0) rot=(0,0,1;1.5708rad)
  LinkedObject = -> Body001
  Placement = pos=(29.5,-89.5001,0) rot=(0,0,1;1.5708rad)
FEATURE [Sketcher::SketchObject] Sketch021
  AttachmentOffset = pos=(0,5,-10) rot=(1,0,0;0.436332rad)
  FullyConstrained = false
  MapMode = 5
  Placement = pos=(0,10,5) rot=(1,0,0;2.00713rad)
  Support = -> [XZ_Plane013]
  sketch-geometry (6):
    g0: Circle CenterX=15.5 CenterY=18.346 CenterZ=0 NormalX=0 NormalY=0 NormalZ=1 AngleXU=0 Radius=2.5
    g1: Circle CenterX=-15.5 CenterY=18.346 CenterZ=0 NormalX=0 NormalY=0 NormalZ=1 AngleXU=0 Radius=2.5
    g2: Circle CenterX=15.5 CenterY=40.846 CenterZ=0 NormalX=0 NormalY=0 NormalZ=1 AngleXU=0 Radius=2.5
    g3: Circle CenterX=-15.5 CenterY=40.846 CenterZ=0 NormalX=0 NormalY=0 NormalZ=1 AngleXU=0 Radius=2.5
    g4: Circle CenterX=-15.5 CenterY=18.346 CenterZ=0 NormalX=0 NormalY=0 NormalZ=1 AngleXU=0 Radius=5.75
    g5: Circle CenterX=15.5 CenterY=18.346 CenterZ=0 NormalX=0 NormalY=0 NormalZ=1 AngleXU=0 Radius=5.75
  constraints (13):
    c: Equal(g3,g1)
    c: Equal(g1,g0)
    c: Equal(g0,g2)
    c: Symmetric(g1,g0,g-2)
    c: Symmetric(g3,g2,g-2)
    c: Vertical(g3,g1)
    c: Coincident(g4,g1)
    c: Coincident(g5,g0)
    c: Diameter(g4) = 11.5
    c: Equal(g4,g5)
    c: DistanceX(g1,g-1) = 15.5
    c: DistanceY(g1,g3) = 22.5
    c: Diameter(g1) = 5
FEATURE [PartDesign::Pocket] Pocket010
  BaseFeature = -> Pocket009
  Direction = (0,0.906308,0.422618)
  Length = 5
  Length2 = 5
  Placement = pos=(0,0,0) rot=(0.57735,0.57735,0.57735;2.0944rad)
  Profile = -> Sketch021
  ReferenceAxis = -> Sketch021 [N_Axis]
  Type = 1
FEATURE [Part::FeaturePython] Screw003  label="M5x8-Screw002"  # Fasteners workbench fastener (typed FeaturePython)
  Placement = pos=(46,-7.56015,24.5267) rot=(-1,0,0;4.27606rad)
  diameter = 4
  invert = false
  leftHanded = false
  length = 1
  lengthCustom = 8
  matchOuter = false
  offset = 0
  thread = false
  type = 17
FEATURE [Sketcher::SketchObject] Sketch022
  FullyConstrained = false
  MapMode = 5
  Support = -> [XY_Plane013]
  sketch-geometry (4):
    g0: LineSegment StartX=-7.9 StartY=-20.1143 StartZ=0 EndX=7.9 EndY=-20.1143 EndZ=0
    g1: LineSegment StartX=7.9 StartY=-20.1143 StartZ=0 EndX=7.37717 EndY=-2.31433 EndZ=0
    g2: LineSegment StartX=7.37717 StartY=-2.31433 StartZ=0 EndX=-7.37717 EndY=-2.31433 EndZ=0
    g3: LineSegment StartX=-7.37717 StartY=-2.31433 StartZ=0 EndX=-7.9 EndY=-20.1143 EndZ=0
  constraints (8):
    c: Coincident(g0,g1)
    c: Coincident(g1,g2)
    c: Coincident(g2,g3)
    c: Coincident(g3,g0)
    c: Symmetric(g0,g0,g-2)
    c: DistanceX(g0,g0) = 15.8
    c: Symmetric(g2,g1,g-2)
    c: DistanceY(g0,g2) = 17.8
FEATURE [PartDesign::Pocket] Pocket011
  BaseFeature = -> Pocket010
  Direction = (0,0,-1)
  Length = 11
  Length2 = 5
  Placement = pos=(0,0,0) rot=(0.57735,0.57735,0.57735;2.0944rad)
  Profile = -> Sketch022
  ReferenceAxis = -> Sketch022 [N_Axis]
  Reversed = true
  Type = 2
FEATURE [PartDesign::Body] Body009  label="RearMnt"
  Group = -> [Sketch016,Pad010,Sketch017,Sketch018,Pocket006,Sketch019,Pocket007,Pocket008,Sketch020,Pocket009,Sketch021,Pocket010,Sketch022,Pocket011]
  Origin = -> Origin013
  Placement = pos=(30.5,-12,2) rot=(0,0,1;0rad)
  Tip = -> Pocket011
FEATURE [App::Part] Part003  label="RearFoot"
  Group = -> [Link001,Body009,Screw002,Link002,Screw003]
  Origin = -> Origin012
  Placement = pos=(234.5,1235.5,16) rot=(0,0,1;0rad)
